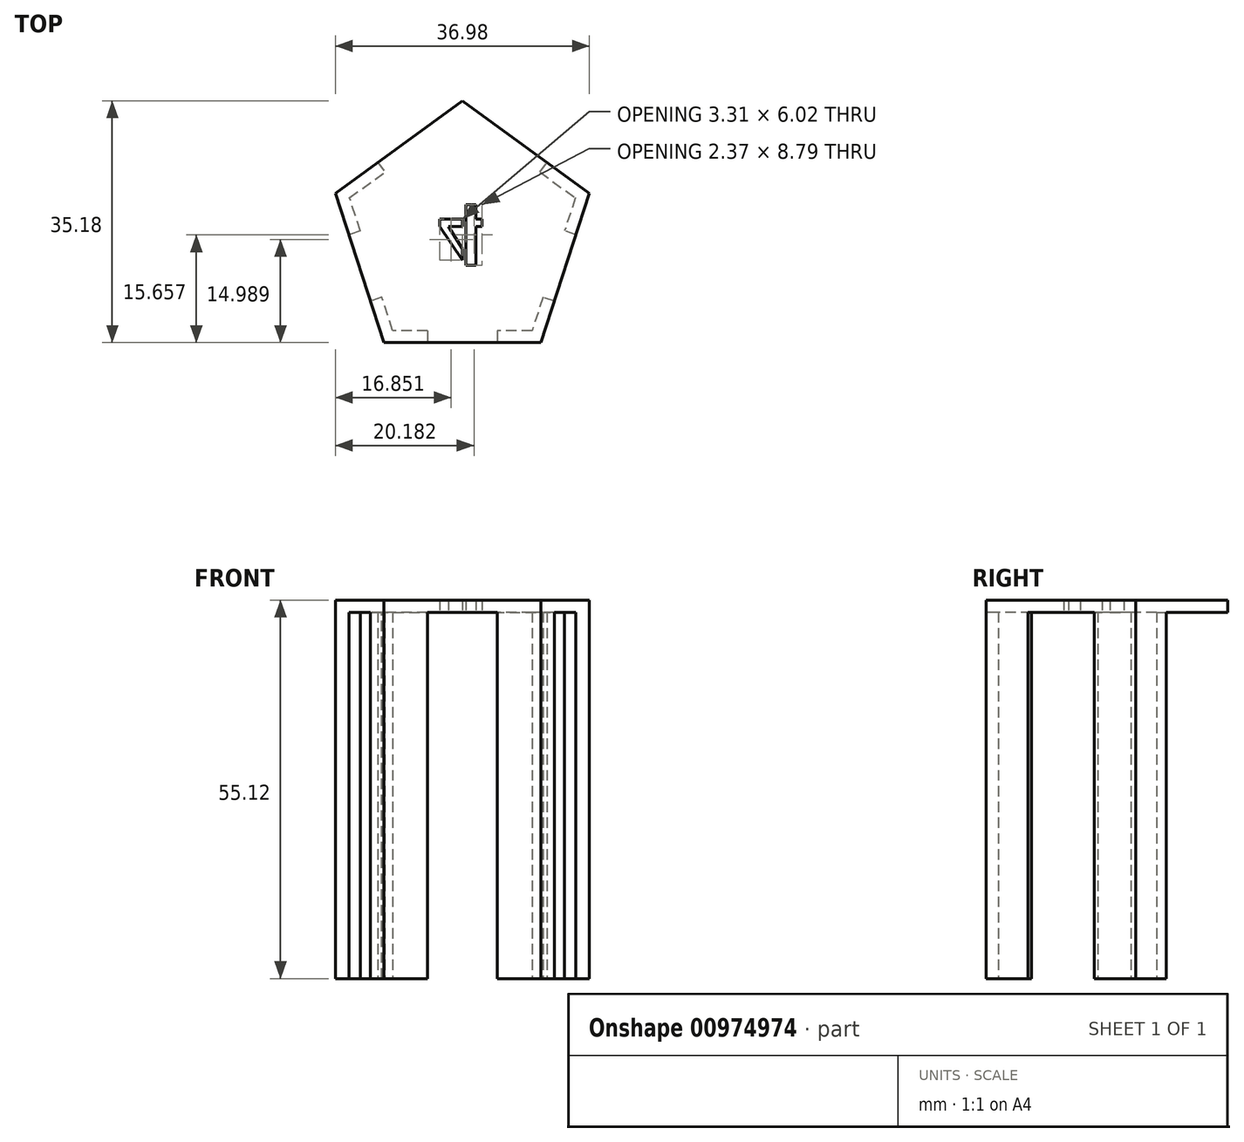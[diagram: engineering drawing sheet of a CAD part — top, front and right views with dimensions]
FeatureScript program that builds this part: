
annotation { "Feature Type Name" : "Feature", "Feature Type Description" : "" }
export const myFeature = defineFeature(function(context is Context, id is Id, definition is map)
    precondition{}
    {
        {
            var Q0;
            Q0=qCreatedBy(makeId("Top.planeOp"),FACE);
            var sketch = newSketch(context, id + "F0", { "sketchPlane" : qUnion([Q0])});
            skCircle(sketch, "E0.cCircle", {"center": v(0, 0) * mm, "radius": 19.45 * mm, "construction": true});
            skLineSegment(sketch, "E0.0", {"start": v(11.43, -15.73) * mm, "end": v(-11.43, -15.73) * mm});
            skLineSegment(sketch, "E0.1", {"start": v(-11.43, -15.73) * mm, "end": v(-18.5, 6) * mm});
            skLineSegment(sketch, "E0.2", {"start": v(-18.5, 6) * mm, "end": v(0, 19.45) * mm});
            skLineSegment(sketch, "E0.3", {"start": v(0, 19.45) * mm, "end": v(18.5, 6) * mm});
            skLineSegment(sketch, "E0.4", {"start": v(18.5, 6) * mm, "end": v(11.43, -15.73) * mm});
            skSolve(sketch);
        }
        {
            var Q0;
            Q0=makeQuery(id+"F0.imprint","IMPRINT",FACE,{"disambiguationData":[TD([[makeQuery(id+"F0.imprint","IMPRINT",EDGE,{"derivedFrom":sQuery(id+"F0.wireOp",EDGE,"E0.0")}),-1.0]])]});
            extrude(context, id + "F1", {"entities" : qUnion([Q0]), "depth" : 55.12 * mm, "offsetDistance" : 25.4 * mm});
        }
        {
            var Q0;
            Q0=qCreatedBy(makeId("Top.planeOp"),FACE);
            var sketch = newSketch(context, id + "F2", { "sketchPlane" : qUnion([Q0])});
            skCircle(sketch, "E1.cCircle", {"center": v(0, 0) * mm, "radius": 13.98 * mm, "construction": true});
            skLineSegment(sketch, "E1.0", {"start": v(16.44, 5.34) * mm, "end": v(10.16, -13.98) * mm});
            skLineSegment(sketch, "E1.1", {"start": v(10.16, -13.98) * mm, "end": v(-10.16, -13.98) * mm});
            skLineSegment(sketch, "E1.2", {"start": v(-10.16, -13.98) * mm, "end": v(-16.44, 5.34) * mm});
            skLineSegment(sketch, "E1.3", {"start": v(-16.44, 5.34) * mm, "end": v(0, 17.29) * mm});
            skLineSegment(sketch, "E1.4", {"start": v(0, 17.29) * mm, "end": v(16.44, 5.34) * mm});
            skPoint(sketch, "E1.0.midPoint", {"position": v(13.3, -4.32) * mm});
            skSolve(sketch);
        }
        {
            var Q0;
            Q0=qSketchRegion(id+"F2",true);
            extrude(context, id + "F3", {"entities" : qUnion([Q0]), "operationType" : NewBodyOperationType.REMOVE, "depth" : 53.34 * mm, "offsetDistance" : 25.4 * mm});
        }
        {
            var Q0;
            Q0=makeQuery(id+"F1.opExtrude","CAP_FACE",FACE,{"disambiguationData":[OSD([sQuery(id+"F0.wireOp",EDGE,"E0.0"),sQuery(id+"F0.wireOp",EDGE,"E0.1"),sQuery(id+"F0.wireOp",EDGE,"E0.2"),sQuery(id+"F0.wireOp",EDGE,"E0.3"),sQuery(id+"F0.wireOp",EDGE,"E0.4")])],"isStart":true});
            var sketch = newSketch(context, id + "F4", { "sketchPlane" : qUnion([Q0])});
            skLineSegment(sketch, "E2", {"start": v(0, 0) * mm, "end": v(23.62, 7.67) * mm});
            skLineSegment(sketch, "E3", {"start": v(0, 0) * mm, "end": v(-35.57, 11.56) * mm});
            skLineSegment(sketch, "E4", {"start": v(0, 0) * mm, "end": v(0, -28.1) * mm});
            skLineSegment(sketch, "E5.bottom", {"start": v(-11.25, -1.69) * mm, "end": v(-18.5, 0.67) * mm});
            skLineSegment(sketch, "E5.top", {"start": v(-8.1, 7.98) * mm, "end": v(-15.35, 10.33) * mm});
            skLineSegment(sketch, "E5.left", {"start": v(-11.25, -1.69) * mm, "end": v(-8.1, 7.98) * mm});
            skLineSegment(sketch, "E5.right", {"start": v(-18.5, 0.67) * mm, "end": v(-15.35, 10.33) * mm});
            skPoint(sketch, "E5.middle", {"position": v(-13.3, 4.32) * mm});
            skLineSegment(sketch, "E6.bottom", {"start": v(18.5, 0.67) * mm, "end": v(11.25, -1.69) * mm});
            skLineSegment(sketch, "E6.top", {"start": v(15.35, 10.33) * mm, "end": v(8.1, 7.98) * mm});
            skLineSegment(sketch, "E6.left", {"start": v(18.5, 0.67) * mm, "end": v(15.35, 10.33) * mm});
            skLineSegment(sketch, "E6.right", {"start": v(11.25, -1.69) * mm, "end": v(8.1, 7.98) * mm});
            skPoint(sketch, "E6.middle", {"position": v(13.3, 4.32) * mm});
            skLineSegment(sketch, "E7.bottom", {"start": v(5.08, 10.17) * mm, "end": v(-5.08, 10.17) * mm});
            skLineSegment(sketch, "E7.top", {"start": v(5.08, 17.8) * mm, "end": v(-5.08, 17.8) * mm});
            skLineSegment(sketch, "E7.left", {"start": v(5.08, 10.17) * mm, "end": v(5.08, 17.8) * mm});
            skLineSegment(sketch, "E7.right", {"start": v(-5.08, 10.17) * mm, "end": v(-5.08, 17.8) * mm});
            skPoint(sketch, "E7.middle", {"position": v(0, 13.98) * mm});
            skLineSegment(sketch, "E8", {"start": v(-12.33, -10.49) * mm, "end": v(-11.3, -9.07) * mm});
            skLineSegment(sketch, "E9", {"start": v(11.3, -9.07) * mm, "end": v(12.33, -10.49) * mm});
            skLineSegment(sketch, "E10", {"start": v(-11.3, -9.07) * mm, "end": v(11.3, -9.07) * mm});
            skLineSegment(sketch, "E11", {"start": v(-12.33, -10.49) * mm, "end": v(0, -28.1) * mm});
            skLineSegment(sketch, "E12", {"start": v(12.33, -10.49) * mm, "end": v(0, -28.1) * mm});
            skSolve(sketch);
        }
        {
            var Q0;
            {var subQ0=sQuery(id+"F4.wireOp",EDGE,"E3");var subQ1=makeQuery(id+"F3.boolean.opBoolean","COPY",EDGE,{"derivedFrom":makeQuery(id+"F3.opExtrude","CAP_EDGE",EDGE,{"disambiguationData":[OSD([sQuery(id+"F2.wireOp",EDGE,"E1.2")])],"isStart":true})});var subQ2=makeQuery(id+"F4.imprint","INTERSECT",VERTEX,{"derivedFrom":[subQ1,subQ0]});Q0=makeQuery(id+"F4.imprint","IMPRINT",FACE,{"disambiguationData":[TD([[makeQuery(id+"F4.imprint","IMPRINT",EDGE,{"disambiguationData":[TD([[subQ2,-1.0]])],"derivedFrom":subQ0}),1.0]])]});}
            var Q1;
            {var subQ0=sQuery(id+"F4.wireOp",EDGE,"E3");var subQ1=makeQuery(id+"F3.boolean.opBoolean","COPY",EDGE,{"derivedFrom":makeQuery(id+"F3.opExtrude","CAP_EDGE",EDGE,{"disambiguationData":[OSD([sQuery(id+"F2.wireOp",EDGE,"E1.2")])],"isStart":true})});var subQ2=makeQuery(id+"F4.imprint","INTERSECT",VERTEX,{"derivedFrom":[subQ1,subQ0]});Q1=makeQuery(id+"F4.imprint","IMPRINT",FACE,{"disambiguationData":[TD([[makeQuery(id+"F4.imprint","IMPRINT",EDGE,{"disambiguationData":[TD([[subQ2,-1.0]])],"derivedFrom":subQ0}),-1.0]])]});}
            var Q2;
            {var subQ0=sQuery(id+"F4.wireOp",EDGE,"E2");var subQ1=makeQuery(id+"F3.boolean.opBoolean","COPY",EDGE,{"derivedFrom":makeQuery(id+"F3.opExtrude","CAP_EDGE",EDGE,{"disambiguationData":[OSD([sQuery(id+"F2.wireOp",EDGE,"E1.0")])],"isStart":true})});var subQ2=makeQuery(id+"F4.imprint","INTERSECT",VERTEX,{"derivedFrom":[subQ1,subQ0]});Q2=makeQuery(id+"F4.imprint","IMPRINT",FACE,{"disambiguationData":[TD([[makeQuery(id+"F4.imprint","IMPRINT",EDGE,{"disambiguationData":[TD([[subQ2,-1.0]])],"derivedFrom":subQ0}),1.0]])]});}
            var Q3;
            {var subQ0=sQuery(id+"F4.wireOp",EDGE,"E2");var subQ1=makeQuery(id+"F3.boolean.opBoolean","COPY",EDGE,{"derivedFrom":makeQuery(id+"F3.opExtrude","CAP_EDGE",EDGE,{"disambiguationData":[OSD([sQuery(id+"F2.wireOp",EDGE,"E1.0")])],"isStart":true})});var subQ2=makeQuery(id+"F4.imprint","INTERSECT",VERTEX,{"derivedFrom":[subQ1,subQ0]});Q3=makeQuery(id+"F4.imprint","IMPRINT",FACE,{"disambiguationData":[TD([[makeQuery(id+"F4.imprint","IMPRINT",EDGE,{"disambiguationData":[TD([[subQ2,-1.0]])],"derivedFrom":subQ0}),-1.0]])]});}
            var Q4;
            {var subQ1=makeQuery(id+"F1.opExtrude","CAP_EDGE",EDGE,{"disambiguationData":[OSD([sQuery(id+"F0.wireOp",EDGE,"E0.2")])],"isStart":true});var subQ5=sQuery(id+"F4.wireOp",EDGE,"VIOiiu8y-qDuE-E9mX-nsSh-dz9hzi8E33ez.right");var subQ6=makeQuery(id+"F4.imprint","INTERSECT",VERTEX,{"derivedFrom":[subQ1,subQ5]});Q4=makeQuery(id+"F4.imprint","IMPRINT",FACE,{"disambiguationData":[TD([[makeQuery(id+"F4.imprint","IMPRINT",EDGE,{"disambiguationData":[TD([[subQ6,-1.0]])],"derivedFrom":subQ5}),-1.0]])]});}
            var Q5;
            {var subQ1=makeQuery(id+"F1.opExtrude","CAP_EDGE",EDGE,{"disambiguationData":[OSD([sQuery(id+"F0.wireOp",EDGE,"E0.3")])],"isStart":true});var subQ5=sQuery(id+"F4.wireOp",EDGE,"VIOiiu8y-qDuE-E9mX-nsSh-dz9hzi8E33ez.left");var subQ6=makeQuery(id+"F4.imprint","INTERSECT",VERTEX,{"derivedFrom":[subQ1,subQ5]});Q5=makeQuery(id+"F4.imprint","IMPRINT",FACE,{"disambiguationData":[TD([[makeQuery(id+"F4.imprint","IMPRINT",EDGE,{"disambiguationData":[TD([[subQ6,-1.0]])],"derivedFrom":subQ5}),1.0]])]});}
            var Q6;
            {var subQ0=sQuery(id+"F4.wireOp",EDGE,"E7.left");var subQ1=makeQuery(id+"F1.opExtrude","CAP_EDGE",EDGE,{"disambiguationData":[OSD([sQuery(id+"F0.wireOp",EDGE,"E0.0")])],"isStart":true});var subQ2=makeQuery(id+"F4.imprint","INTERSECT",VERTEX,{"derivedFrom":[subQ1,subQ0]});Q6=makeQuery(id+"F4.imprint","IMPRINT",FACE,{"disambiguationData":[TD([[makeQuery(id+"F4.imprint","IMPRINT",EDGE,{"disambiguationData":[TD([[subQ2,1.0]])],"derivedFrom":subQ0}),1.0]])]});}
            var Q7;
            {var subQ5=sQuery(id+"F4.wireOp",EDGE,"E8");Q7=makeQuery(id+"F4.imprint","IMPRINT",FACE,{"disambiguationData":[TD([[makeQuery(id+"F4.imprint","IMPRINT",EDGE,{"derivedFrom":subQ5}),-1.0]])]});}
            var Q8;
            {var subQ5=sQuery(id+"F4.wireOp",EDGE,"E9");Q8=makeQuery(id+"F4.imprint","IMPRINT",FACE,{"disambiguationData":[TD([[makeQuery(id+"F4.imprint","IMPRINT",EDGE,{"derivedFrom":subQ5}),-1.0]])]});}
            extrude(context, id + "F5", {"entities" : qUnion([Q0, Q1, Q2, Q3, Q4, Q5, Q6, Q7, Q8]), "operationType" : NewBodyOperationType.REMOVE, "oppositeDirection" : true, "depth" : 53.34 * mm, "offsetDistance" : 25.4 * mm});
        }
        {
            var Q0;
            {var subQ0=sQuery(id+"F2.wireOp",EDGE,"E1.4");var subQ1=sQuery(id+"F2.wireOp",EDGE,"E1.3");var subQ2=sQuery(id+"F2.wireOp",EDGE,"E1.1");var subQ3=sQuery(id+"F2.wireOp",EDGE,"E1.0");var subQ4=sQuery(id+"F2.wireOp",EDGE,"E1.2");Q0=makeQuery(id+"F5.boolean.opBoolean","MERGE",FACE,{"derivedFrom":[makeQuery(id+"F3.boolean.opBoolean","COPY",FACE,{"derivedFrom":makeQuery(id+"F3.opExtrude","CAP_FACE",FACE,{"disambiguationData":[OSD([subQ3,subQ2,subQ4,subQ1,subQ0])],"isStart":false})})],"fromTools":[makeQuery(id+"F5.opExtrude","CAP_FACE",FACE,{"disambiguationData":[OSD([sQuery(id+"F0.wireOp",EDGE,"E0.1"),subQ4,sQuery(id+"F4.wireOp",EDGE,"E5.bottom"),sQuery(id+"F4.wireOp",EDGE,"E5.top")])],"isStart":false}),makeQuery(id+"F5.opExtrude","CAP_FACE",FACE,{"disambiguationData":[OSD([sQuery(id+"F0.wireOp",EDGE,"E0.4"),subQ3,sQuery(id+"F4.wireOp",EDGE,"E6.bottom"),sQuery(id+"F4.wireOp",EDGE,"E6.top")])],"isStart":false}),makeQuery(id+"F5.opExtrude","CAP_FACE",FACE,{"disambiguationData":[OSD([sQuery(id+"F0.wireOp",EDGE,"E0.0"),subQ2,sQuery(id+"F4.wireOp",EDGE,"E7.left"),sQuery(id+"F4.wireOp",EDGE,"E7.right")])],"isStart":false}),makeQuery(id+"F5.opExtrude","CAP_FACE",FACE,{"disambiguationData":[OSD([sQuery(id+"F0.wireOp",EDGE,"E0.2"),sQuery(id+"F0.wireOp",EDGE,"E0.3"),subQ1,subQ0,sQuery(id+"F4.wireOp",EDGE,"E8"),sQuery(id+"F4.wireOp",EDGE,"E9")])],"isStart":false})]});}
            var sketch = newSketch(context, id + "F6", { "sketchPlane" : qUnion([Q0])});
            skText(sketch, "E13", { "text": "4\n", "fontName": "AllertaStencil-Regular.ttf"});
            const initialGuessF6  = {"E13": [-0.00375, -0.00432, 1, 0, 0.00879]};
            skSetInitialGuess(sketch, initialGuessF6);
            skSolve(sketch);
        }
        {
            var Q0;
            Q0=makeQuery(id+"F6.imprint","IMPRINT",FACE,{"disambiguationData":[TD([[makeQuery(id+"F6.imprint","IMPRINT",EDGE,{"derivedFrom":sQuery(id+"F6.wireOp",EDGE,"E13.sketch_text.stroke-0")}),-1.0]])]});
            var Q1;
            Q1=makeQuery(id+"F6.imprint","IMPRINT",FACE,{"disambiguationData":[TD([[makeQuery(id+"F6.imprint","IMPRINT",EDGE,{"derivedFrom":sQuery(id+"F6.wireOp",EDGE,"E13.sketch_text.stroke-8")}),-1.0]])]});
            extrude(context, id + "F7", {"entities" : qUnion([Q0, Q1]), "operationType" : NewBodyOperationType.REMOVE, "oppositeDirection" : true, "depth" : 25.4 * mm, "offsetDistance" : 25.4 * mm});
        }
    });
